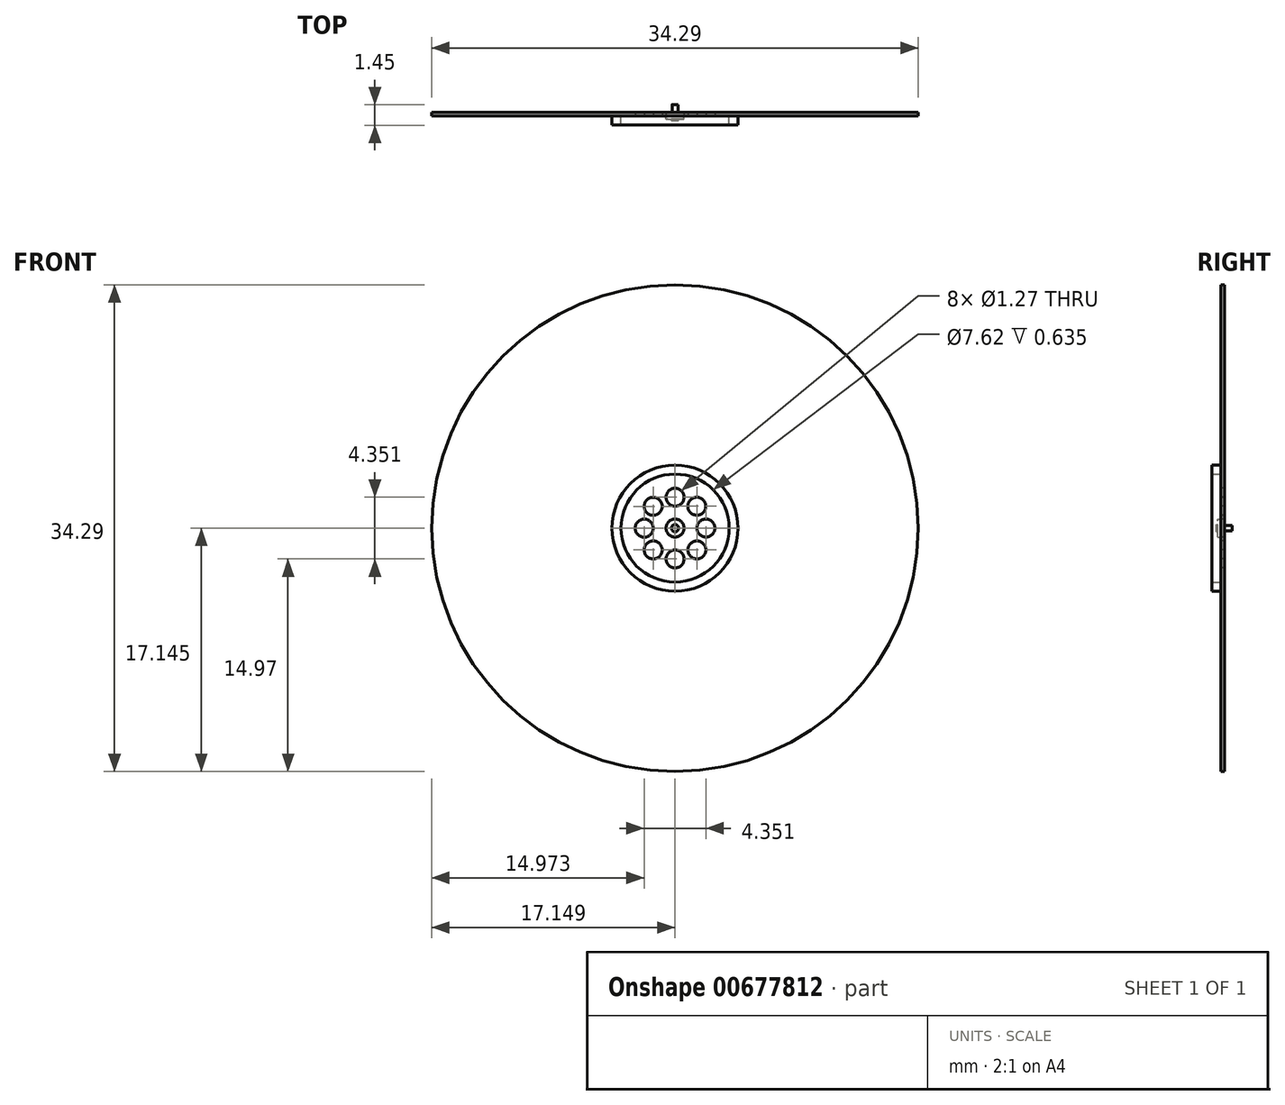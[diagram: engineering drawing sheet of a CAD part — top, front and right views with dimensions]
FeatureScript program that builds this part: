
annotation { "Feature Type Name" : "Feature", "Feature Type Description" : "" }
export const myFeature = defineFeature(function(context is Context, id is Id, definition is map)
    precondition{}
    {
        {
            var Q0;
            Q0=qCreatedBy(makeId("Front.planeOp"),FACE);
            var sketch = newSketch(context, id + "F0", { "sketchPlane" : qUnion([Q0])});
            skCircle(sketch, "E0", {"center": v(-30.86, 27.3) * mm, "radius": 17.15 * mm});
            skSolve(sketch);
        }
        {
            var Q0;
            Q0=makeQuery(id+"F0.imprint","IMPRINT",FACE,{"disambiguationData":[TD([[makeQuery(id+"F0.imprint","IMPRINT",EDGE,{"derivedFrom":sQuery(id+"F0.wireOp",EDGE,"E0")}),1.0]])]});
            extrude(context, id + "F1", {"entities" : qUnion([Q0]), "oppositeDirection" : true, "depth" : 0.25 * mm, "offsetDistance" : 25.4 * mm});
        }
        {
            var Q0;
            Q0=qCreatedBy(makeId("Front.planeOp"),FACE);
            var sketch = newSketch(context, id + "F2", { "sketchPlane" : qUnion([Q0])});
            skCircle(sketch, "E1", {"center": v(-30.86, 27.3) * mm, "radius": 4.45 * mm});
            skCircle(sketch, "E2", {"center": v(-30.86, 27.3) * mm, "radius": 3.81 * mm});
            skSolve(sketch);
        }
        {
            var Q0;
            Q0 = qSketchRegion(id + "F2", true);
            extrude(context, id + "F3", {"entities" : qUnion([Q0]), "operationType" : NewBodyOperationType.ADD, "depth" : 0.64 * mm, "offsetDistance" : 25.4 * mm});
        }
        {
            var Q0;
            Q0=makeQuery(id+"F0.imprint","IMPRINT",FACE,{"disambiguationData":[TD([[makeQuery(id+"F0.imprint","IMPRINT",EDGE,{"derivedFrom":sQuery(id+"F0.wireOp",EDGE,"E0")}),1.0]])]});
            var sketch = newSketch(context, id + "F4", { "sketchPlane" : qUnion([Q0])});
            skCircle(sketch, "E3", {"center": v(-30.86, 27.3) * mm, "radius": 0.64 * mm});
            skSolve(sketch);
        }
        {
            var Q0;
            Q0=makeQuery(id+"F4.imprint","IMPRINT",FACE,{"disambiguationData":[TD([[makeQuery(id+"F4.imprint","IMPRINT",EDGE,{"derivedFrom":sQuery(id+"F4.wireOp",EDGE,"E3")}),1.0]])]});
            extrude(context, id + "F5", {"entities" : qUnion([Q0]), "operationType" : NewBodyOperationType.ADD, "depth" : 0.2 * mm, "offsetDistance" : 25.4 * mm});
        }
        {
            var Q0;
            Q0=makeQuery(id+"F5.opExtrude","CAP_FACE",FACE,{"disambiguationData":[OSD([sQuery(id+"F4.wireOp",EDGE,"E3")])],"isStart":false});
            var sketch = newSketch(context, id + "F6", { "sketchPlane" : qUnion([Q0])});
            skCircle(sketch, "E4", {"center": v(-30.86, 27.3) * mm, "radius": 0.25 * mm});
            skSolve(sketch);
        }
        {
            var Q0;
            Q0=makeQuery(id+"F6.imprint","IMPRINT",FACE,{"disambiguationData":[TD([[makeQuery(id+"F6.imprint","IMPRINT",EDGE,{"derivedFrom":sQuery(id+"F6.wireOp",EDGE,"E4")}),1.0]])]});
            extrude(context, id + "F7", {"entities" : qUnion([Q0]), "operationType" : NewBodyOperationType.ADD, "depth" : 0.1 * mm, "offsetDistance" : 25.4 * mm});
        }
        {
            var Q0;
            Q0=makeQuery(id+"F3.opExtrude","CAP_FACE",FACE,{"disambiguationData":[OSD([sQuery(id+"F2.wireOp",EDGE,"E1"),sQuery(id+"F2.wireOp",EDGE,"E2")])],"isStart":false});
            var sketch = newSketch(context, id + "F8", { "sketchPlane" : qUnion([Q0])});
            skCircle(sketch, "E5", {"center": v(-30.86, 29.48) * mm, "radius": 0.64 * mm});
            skCircle(sketch, "E6.1.0", {"center": v(-32.4, 28.84) * mm, "radius": 0.64 * mm});
            skCircle(sketch, "E6.2.0", {"center": v(-33.04, 27.3) * mm, "radius": 0.64 * mm});
            skCircle(sketch, "E6.3.0", {"center": v(-32.4, 25.76) * mm, "radius": 0.64 * mm});
            skCircle(sketch, "E6.4.0", {"center": v(-30.86, 25.13) * mm, "radius": 0.64 * mm});
            skCircle(sketch, "E6.5.0", {"center": v(-29.32, 25.77) * mm, "radius": 0.64 * mm});
            skCircle(sketch, "E6.6.0", {"center": v(-28.69, 27.3) * mm, "radius": 0.64 * mm});
            skCircle(sketch, "E6.7.0", {"center": v(-29.33, 28.85) * mm, "radius": 0.64 * mm});
            skPoint(sketch, "E6.center", {"position": v(-30.86, 27.3) * mm});
            skSolve(sketch);
        }
        {
            var Q0;
            Q0=makeQuery(id+"F8.imprint","IMPRINT",FACE,{"disambiguationData":[TD([[makeQuery(id+"F8.imprint","IMPRINT",EDGE,{"derivedFrom":sQuery(id+"F8.wireOp",EDGE,"E5")}),1.0]])]});
            var Q1;
            Q1=makeQuery(id+"F8.imprint","IMPRINT",FACE,{"disambiguationData":[TD([[makeQuery(id+"F8.imprint","IMPRINT",EDGE,{"derivedFrom":sQuery(id+"F8.wireOp",EDGE,"E6.7.0")}),1.0]])]});
            var Q2;
            Q2=makeQuery(id+"F8.imprint","IMPRINT",FACE,{"disambiguationData":[TD([[makeQuery(id+"F8.imprint","IMPRINT",EDGE,{"derivedFrom":sQuery(id+"F8.wireOp",EDGE,"E6.6.0")}),1.0]])]});
            var Q3;
            Q3=makeQuery(id+"F8.imprint","IMPRINT",FACE,{"disambiguationData":[TD([[makeQuery(id+"F8.imprint","IMPRINT",EDGE,{"derivedFrom":sQuery(id+"F8.wireOp",EDGE,"E6.5.0")}),1.0]])]});
            var Q4;
            Q4=makeQuery(id+"F8.imprint","IMPRINT",FACE,{"disambiguationData":[TD([[makeQuery(id+"F8.imprint","IMPRINT",EDGE,{"derivedFrom":sQuery(id+"F8.wireOp",EDGE,"E6.4.0")}),1.0]])]});
            var Q5;
            Q5=makeQuery(id+"F8.imprint","IMPRINT",FACE,{"disambiguationData":[TD([[makeQuery(id+"F8.imprint","IMPRINT",EDGE,{"derivedFrom":sQuery(id+"F8.wireOp",EDGE,"E6.2.0")}),1.0]])]});
            var Q6;
            Q6=makeQuery(id+"F8.imprint","IMPRINT",FACE,{"disambiguationData":[TD([[makeQuery(id+"F8.imprint","IMPRINT",EDGE,{"derivedFrom":sQuery(id+"F8.wireOp",EDGE,"E6.1.0")}),1.0]])]});
            var Q7;
            Q7=makeQuery(id+"F8.imprint","IMPRINT",FACE,{"disambiguationData":[TD([[makeQuery(id+"F8.imprint","IMPRINT",EDGE,{"derivedFrom":sQuery(id+"F8.wireOp",EDGE,"E6.3.0")}),1.0]])]});
            extrude(context, id + "F9", {"entities" : qUnion([Q0, Q1, Q2, Q3, Q4, Q5, Q6, Q7]), "operationType" : NewBodyOperationType.REMOVE, "oppositeDirection" : true, "depth" : 1.88 * mm, "offsetDistance" : 25.4 * mm});
        }
        {
            var Q0;
            Q0=makeQuery(id+"F1.opExtrude","CAP_FACE",FACE,{"disambiguationData":[OSD([sQuery(id+"F0.wireOp",EDGE,"E0")])],"isStart":false});
            var sketch = newSketch(context, id + "F10", { "sketchPlane" : qUnion([Q0])});
            skCircle(sketch, "E7", {"center": v(30.86, 27.3) * mm, "radius": 0.2 * mm});
            skSolve(sketch);
        }
        {
            var Q0;
            Q0=makeQuery(id+"F10.imprint","IMPRINT",FACE,{"disambiguationData":[TD([[makeQuery(id+"F10.imprint","IMPRINT",EDGE,{"derivedFrom":sQuery(id+"F10.wireOp",EDGE,"E7")}),1.0]])]});
            extrude(context, id + "F11", {"entities" : qUnion([Q0]), "operationType" : NewBodyOperationType.ADD, "depth" : 0.56 * mm, "offsetDistance" : 25.4 * mm});
        }
    });
